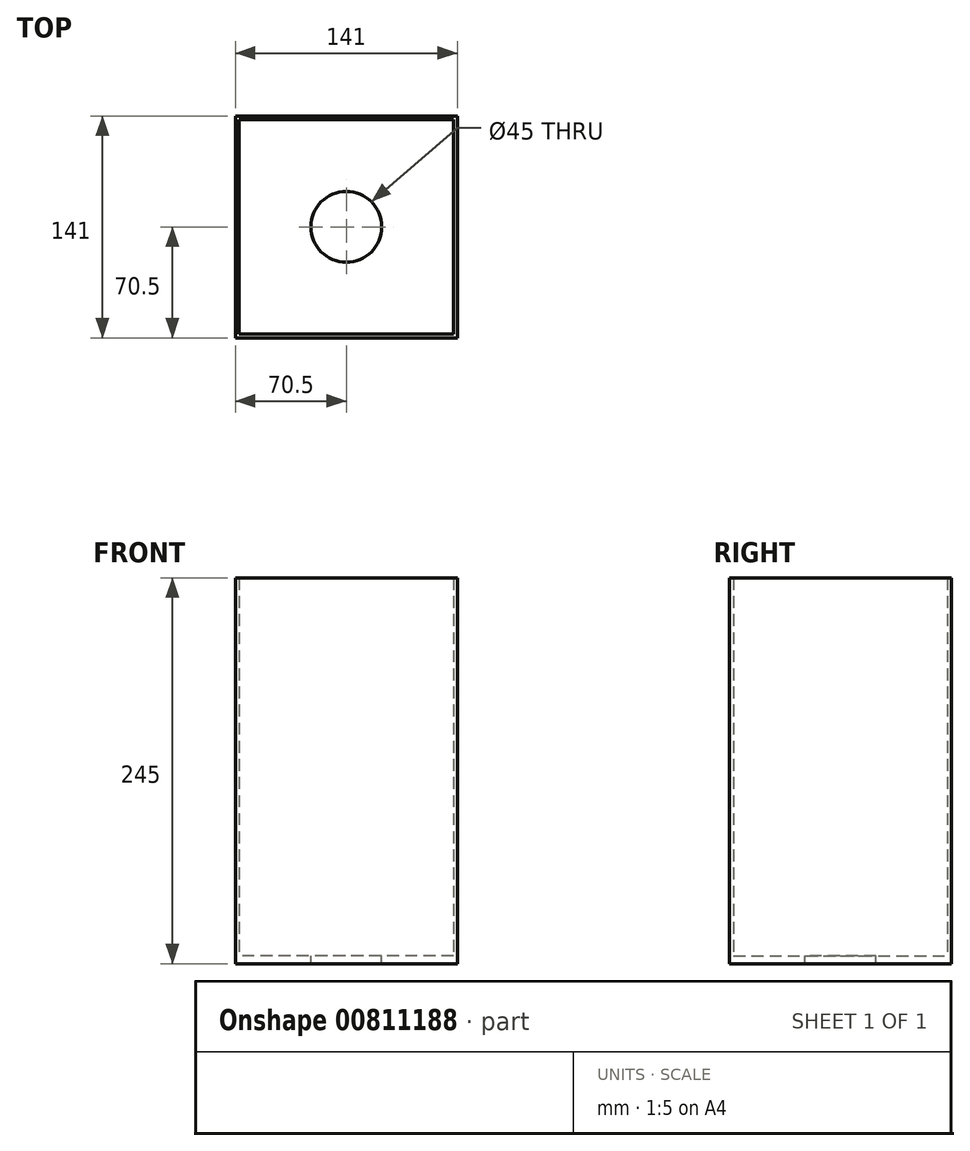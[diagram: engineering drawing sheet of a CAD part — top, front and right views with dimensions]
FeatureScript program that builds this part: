
annotation { "Feature Type Name" : "Feature", "Feature Type Description" : "" }
export const myFeature = defineFeature(function(context is Context, id is Id, definition is map)
    precondition{}
    {
        {
            var Q0;
            Q0=qCreatedBy(makeId("Top.planeOp"),FACE);
            var sketch = newSketch(context, id + "F0", { "sketchPlane" : qUnion([Q0])});
            skLineSegment(sketch, "E0.bottom", {"start": v(-70.5, 70.5) * mm, "end": v(70.5, 70.5) * mm});
            skLineSegment(sketch, "E0.top", {"start": v(-70.5, -70.5) * mm, "end": v(70.5, -70.5) * mm});
            skLineSegment(sketch, "E0.left", {"start": v(-70.5, 70.5) * mm, "end": v(-70.5, -70.5) * mm});
            skLineSegment(sketch, "E0.right", {"start": v(70.5, 70.5) * mm, "end": v(70.5, -70.5) * mm});
            skPoint(sketch, "E0.middle", {"position": v(0, 0) * mm});
            skLineSegment(sketch, "E1.bottom", {"start": v(-68, 68) * mm, "end": v(68, 68) * mm});
            skLineSegment(sketch, "E1.top", {"start": v(-68, -68) * mm, "end": v(68, -68) * mm});
            skLineSegment(sketch, "E1.left", {"start": v(-68, 68) * mm, "end": v(-68, -68) * mm});
            skLineSegment(sketch, "E1.right", {"start": v(68, 68) * mm, "end": v(68, -68) * mm});
            skSolve(sketch);
        }
        {
            var Q0;
            Q0=makeQuery(id+"F0.imprint","IMPRINT",FACE,{"disambiguationData":[TD([[makeQuery(id+"F0.imprint","IMPRINT",EDGE,{"derivedFrom":sQuery(id+"F0.wireOp",EDGE,"E0.bottom")}),-1.0]])]});
            var Q1;
            Q1=makeQuery(id+"F0.imprint","IMPRINT",FACE,{"disambiguationData":[TD([[makeQuery(id+"F0.imprint","IMPRINT",EDGE,{"derivedFrom":sQuery(id+"F0.wireOp",EDGE,"E1.bottom")}),-1.0]])]});
            extrude(context, id + "F1", {"entities" : qUnion([Q0, Q1]), "depth" : 5 * mm, "offsetDistance" : 25 * mm});
        }
        {
            var Q0;
            Q0 = qSketchRegion(id + "F0", true);
            extrude(context, id + "F2", {"entities" : qUnion([Q0]), "operationType" : NewBodyOperationType.ADD, "depth" : 245 * mm, "offsetDistance" : 25 * mm});
        }
        {
            var Q0;
            Q0=makeQuery(id+"F1.opExtrude","CAP_FACE",FACE,{"disambiguationData":[OSD([sQuery(id+"F0.wireOp",EDGE,"E0.bottom"),sQuery(id+"F0.wireOp",EDGE,"E0.top"),sQuery(id+"F0.wireOp",EDGE,"E0.left"),sQuery(id+"F0.wireOp",EDGE,"E0.right")])],"isStart":false});
            var sketch = newSketch(context, id + "F3", { "sketchPlane" : qUnion([Q0])});
            skCircle(sketch, "E2", {"center": v(0, 0) * mm, "radius": 22.5 * mm});
            skSolve(sketch);
        }
        {
            var Q0;
            Q0=makeQuery(id+"F3.imprint","IMPRINT",FACE,{"disambiguationData":[TD([[makeQuery(id+"F3.imprint","IMPRINT",EDGE,{"derivedFrom":sQuery(id+"F3.wireOp",EDGE,"E2")}),1.0]])]});
            extrude(context, id + "F4", {"entities" : qUnion([Q0]), "operationType" : NewBodyOperationType.REMOVE, "oppositeDirection" : true, "depth" : 25 * mm, "offsetDistance" : 25 * mm});
        }
    });
